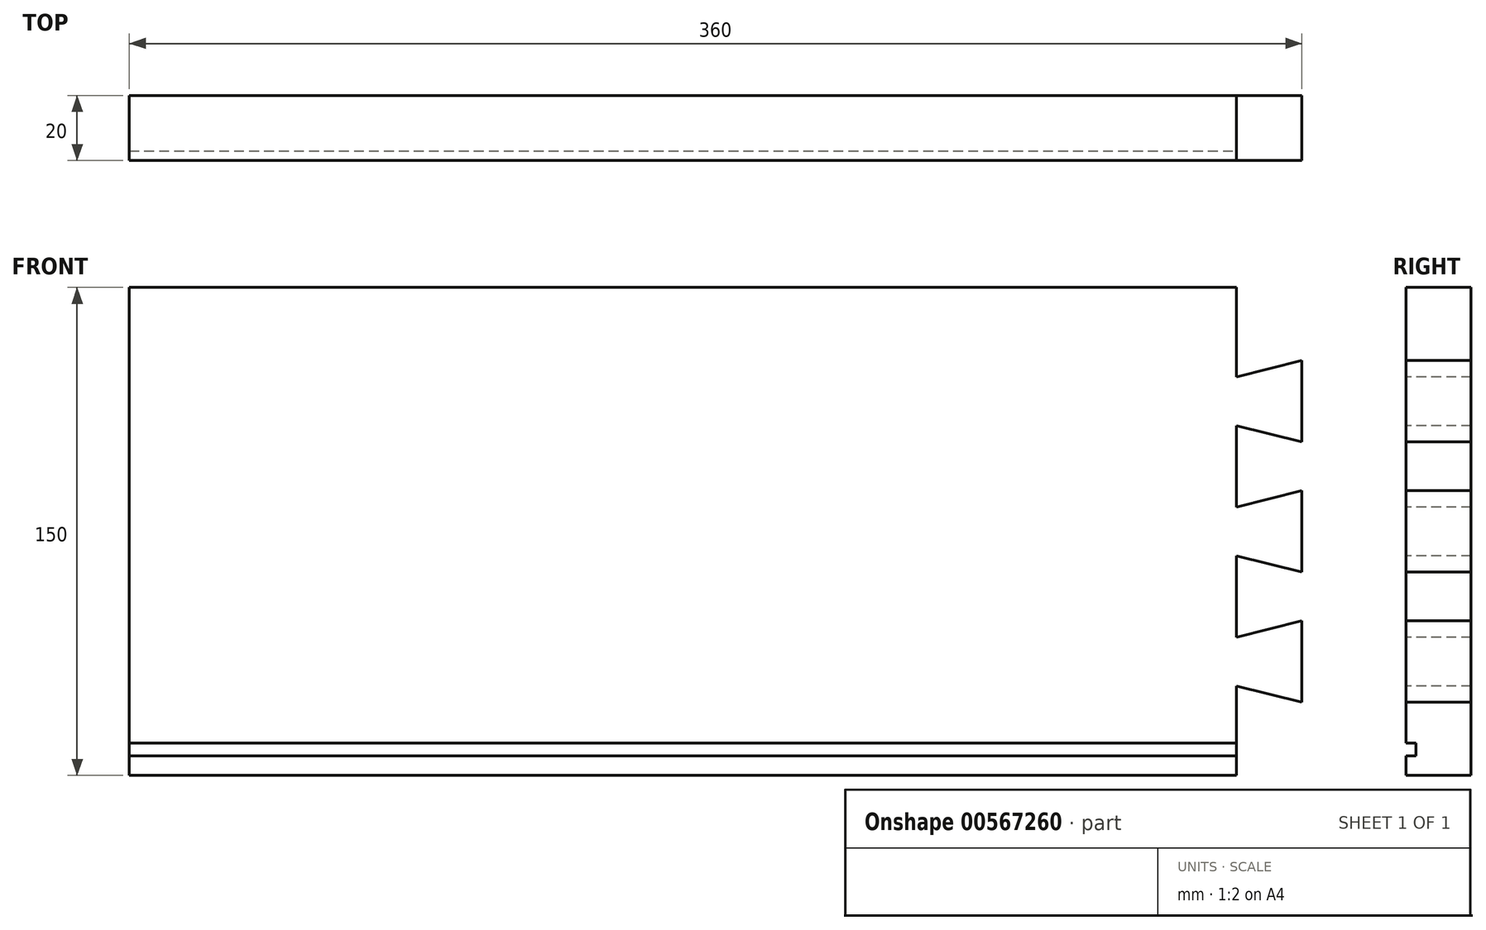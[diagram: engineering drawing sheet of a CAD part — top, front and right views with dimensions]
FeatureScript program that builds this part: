
annotation { "Feature Type Name" : "Feature", "Feature Type Description" : "" }
export const myFeature = defineFeature(function(context is Context, id is Id, definition is map)
    precondition{}
    {
        {
            var Q0;
            Q0=qCreatedBy(makeId("Front.planeOp"),FACE);
            var sketch = newSketch(context, id + "F0", { "sketchPlane" : qUnion([Q0])});
            skLineSegment(sketch, "E0.bottom", {"start": v(-187.76, 20.29) * mm, "end": v(172.24, 20.29) * mm});
            skLineSegment(sketch, "E0.top", {"start": v(-187.76, -129.71) * mm, "end": v(172.24, -129.71) * mm});
            skLineSegment(sketch, "E0.left", {"start": v(-187.76, 20.29) * mm, "end": v(-187.76, -129.71) * mm});
            skLineSegment(sketch, "E0.right", {"start": v(172.24, 20.29) * mm, "end": v(172.24, -129.71) * mm});
            skSolve(sketch);
        }
        {
            var Q0;
            Q0=makeQuery(id+"F0.imprint","IMPRINT",FACE,{"disambiguationData":[TD([[makeQuery(id+"F0.imprint","IMPRINT",EDGE,{"derivedFrom":sQuery(id+"F0.wireOp",EDGE,"E0.bottom")}),-1.0]])]});
            extrude(context, id + "F1", {"entities" : qUnion([Q0]), "depth" : 20 * mm, "offsetDistance" : 25 * mm});
        }
        {
            var Q0;
            Q0=makeQuery(id+"F1.opExtrude","CAP_FACE",FACE,{"disambiguationData":[OSD([sQuery(id+"F0.wireOp",EDGE,"E0.bottom"),sQuery(id+"F0.wireOp",EDGE,"E0.top"),sQuery(id+"F0.wireOp",EDGE,"E0.left"),sQuery(id+"F0.wireOp",EDGE,"E0.right")])],"isStart":false});
            var sketch = newSketch(context, id + "F2", { "sketchPlane" : qUnion([Q0])});
            skLineSegment(sketch, "E1", {"start": v(152.24, 20.29) * mm, "end": v(152.24, -129.71) * mm});
            skLineSegment(sketch, "E2", {"start": v(152.24, -54.71) * mm, "end": v(172.24, -54.71) * mm});
            skLineSegment(sketch, "E3", {"start": v(152.24, -54.71) * mm, "end": v(152.24, -47.21) * mm});
            skLineSegment(sketch, "E4", {"start": v(172.24, -54.71) * mm, "end": v(172.24, -42.21) * mm});
            skLineSegment(sketch, "E5", {"start": v(152.24, -47.21) * mm, "end": v(172.24, -42.21) * mm});
            skLineSegment(sketch, "E6", {"start": v(152.24, -47.21) * mm, "end": v(152.24, -22.21) * mm});
            skLineSegment(sketch, "E7", {"start": v(172.24, -42.21) * mm, "end": v(172.24, -27.21) * mm});
            skLineSegment(sketch, "E8", {"start": v(152.24, -22.21) * mm, "end": v(172.24, -27.21) * mm});
            skLineSegment(sketch, "E9", {"start": v(172.24, -27.21) * mm, "end": v(172.24, -2.21) * mm});
            skLineSegment(sketch, "E10", {"start": v(172.24, -2.21) * mm, "end": v(152.24, -7.22) * mm});
            skLineSegment(sketch, "E11", {"start": v(172.24, -2.21) * mm, "end": v(172.24, 12.79) * mm});
            skLineSegment(sketch, "E12", {"start": v(172.24, 12.79) * mm, "end": v(152.24, 17.79) * mm});
            skLineSegment(sketch, "E13.MirrorCS", {"start": v(152.24, -62.21) * mm, "end": v(172.24, -67.21) * mm});
            skLineSegment(sketch, "E14.MirrorCS", {"start": v(152.24, -87.21) * mm, "end": v(172.24, -82.21) * mm});
            skLineSegment(sketch, "E15.MirrorCS", {"start": v(172.24, -107.21) * mm, "end": v(152.24, -102.21) * mm});
            skLineSegment(sketch, "E16.MirrorCS", {"start": v(172.24, -122.21) * mm, "end": v(152.24, -127.22) * mm});
            skLineSegment(sketch, "E17.MirrorCS", {"start": v(152.24, -54.71) * mm, "end": v(152.24, -62.21) * mm});
            skLineSegment(sketch, "E18.MirrorCS", {"start": v(172.24, -54.71) * mm, "end": v(172.24, -67.21) * mm});
            skLineSegment(sketch, "E19.MirrorCS", {"start": v(152.24, -62.21) * mm, "end": v(152.24, -87.21) * mm});
            skLineSegment(sketch, "E20.MirrorCS", {"start": v(172.24, -67.21) * mm, "end": v(172.24, -82.21) * mm});
            skLineSegment(sketch, "E21.MirrorCS", {"start": v(172.24, -82.21) * mm, "end": v(172.24, -107.21) * mm});
            skLineSegment(sketch, "E22.MirrorCS", {"start": v(172.24, -107.21) * mm, "end": v(172.24, -122.21) * mm});
            skSolve(sketch);
        }
        {
            var Q0;
            Q0=makeQuery(id+"F2.imprint","IMPRINT",FACE,{"disambiguationData":[TD([[makeQuery(id+"F2.imprint","IMPRINT",EDGE,{"derivedFrom":sQuery(id+"F2.wireOp",EDGE,"E5")}),1.0]])]});
            var Q1;
            Q1=makeQuery(id+"F2.imprint","IMPRINT",FACE,{"disambiguationData":[TD([[makeQuery(id+"F2.imprint","IMPRINT",EDGE,{"derivedFrom":sQuery(id+"F2.wireOp",EDGE,"E13.MirrorCS")}),-1.0]])]});
            var Q2;
            {var subQ0=sQuery(id+"F2.wireOp",EDGE,"E15.MirrorCS");Q2=makeQuery(id+"F2.imprint","IMPRINT",FACE,{"disambiguationData":[TD([[makeQuery(id+"F2.imprint","IMPRINT",EDGE,{"derivedFrom":subQ0}),1.0]])]});}
            var Q3;
            {var subQ0=sQuery(id+"F2.wireOp",EDGE,"E10");Q3=makeQuery(id+"F2.imprint","IMPRINT",FACE,{"disambiguationData":[TD([[makeQuery(id+"F2.imprint","IMPRINT",EDGE,{"derivedFrom":subQ0}),-1.0]])]});}
            var Q4;
            {var subQ3=sQuery(id+"F2.wireOp",EDGE,"E12");Q4=makeQuery(id+"F2.imprint","IMPRINT",FACE,{"disambiguationData":[TD([[makeQuery(id+"F2.imprint","IMPRINT",EDGE,{"derivedFrom":subQ3}),-1.0]])]});}
            var Q5;
            {var subQ3=sQuery(id+"F2.wireOp",EDGE,"E16.MirrorCS");Q5=makeQuery(id+"F2.imprint","IMPRINT",FACE,{"disambiguationData":[TD([[makeQuery(id+"F2.imprint","IMPRINT",EDGE,{"derivedFrom":subQ3}),1.0]])]});}
            extrude(context, id + "F3", {"entities" : qUnion([Q0, Q1, Q2, Q3, Q4, Q5]), "operationType" : NewBodyOperationType.REMOVE, "oppositeDirection" : true, "depth" : 20 * mm, "offsetDistance" : 25 * mm});
        }
        {
            var Q0;
            Q0=makeQuery(id+"F1.opExtrude","CAP_FACE",FACE,{"disambiguationData":[OSD([sQuery(id+"F0.wireOp",EDGE,"E0.bottom"),sQuery(id+"F0.wireOp",EDGE,"E0.top"),sQuery(id+"F0.wireOp",EDGE,"E0.left"),sQuery(id+"F0.wireOp",EDGE,"E0.right")])],"isStart":false});
            var sketch = newSketch(context, id + "F4", { "sketchPlane" : qUnion([Q0])});
            skLineSegment(sketch, "E23", {"start": v(-187.76, -123.71) * mm, "end": v(152.24, -123.71) * mm});
            skLineSegment(sketch, "E24", {"start": v(152.24, -119.71) * mm, "end": v(-187.76, -119.71) * mm});
            skLineSegment(sketch, "E25", {"start": v(152.24, -119.71) * mm, "end": v(152.24, -123.71) * mm});
            skLineSegment(sketch, "E26", {"start": v(-187.76, -119.71) * mm, "end": v(-187.76, -123.71) * mm});
            skSolve(sketch);
        }
        {
            var Q0;
            Q0=makeQuery(id+"F4.imprint","IMPRINT",FACE,{"disambiguationData":[TD([[makeQuery(id+"F4.imprint","IMPRINT",EDGE,{"derivedFrom":sQuery(id+"F4.wireOp",EDGE,"E23")}),1.0]])]});
            extrude(context, id + "F5", {"entities" : qUnion([Q0]), "operationType" : NewBodyOperationType.REMOVE, "oppositeDirection" : true, "depth" : 3 * mm, "offsetDistance" : 25 * mm});
        }
        {
            var Q0;
            {var subQ2=sQuery(id+"F0.wireOp",EDGE,"E0.top");var subQ5=sQuery(id+"F0.wireOp",EDGE,"E0.bottom");var subQ6=sQuery(id+"F0.wireOp",EDGE,"E0.left");var subQ7=sQuery(id+"F0.wireOp",EDGE,"E0.right");Q0=makeQuery(id+"F5.boolean.opBoolean","SPLIT",FACE,{"disambiguationData":[TD([makeQuery(id+"F1.opExtrude","SWEPT_FACE",FACE,{"disambiguationData":[OSD([subQ5])]})])],"derivedFrom":makeQuery(id+"F1.opExtrude","CAP_FACE",FACE,{"disambiguationData":[OSD([subQ5,subQ2,subQ6,subQ7])],"isStart":false})});}
            var sketch = newSketch(context, id + "F6", { "sketchPlane" : qUnion([Q0])});
            skLineSegment(sketch, "E27", {"start": v(152.24, -87.21) * mm, "end": v(152.24, -102.21) * mm});
            skLineSegment(sketch, "E28", {"start": v(162.24, -104.71) * mm, "end": v(162.24, -84.71) * mm});
            skSolve(sketch);
        }
    });
